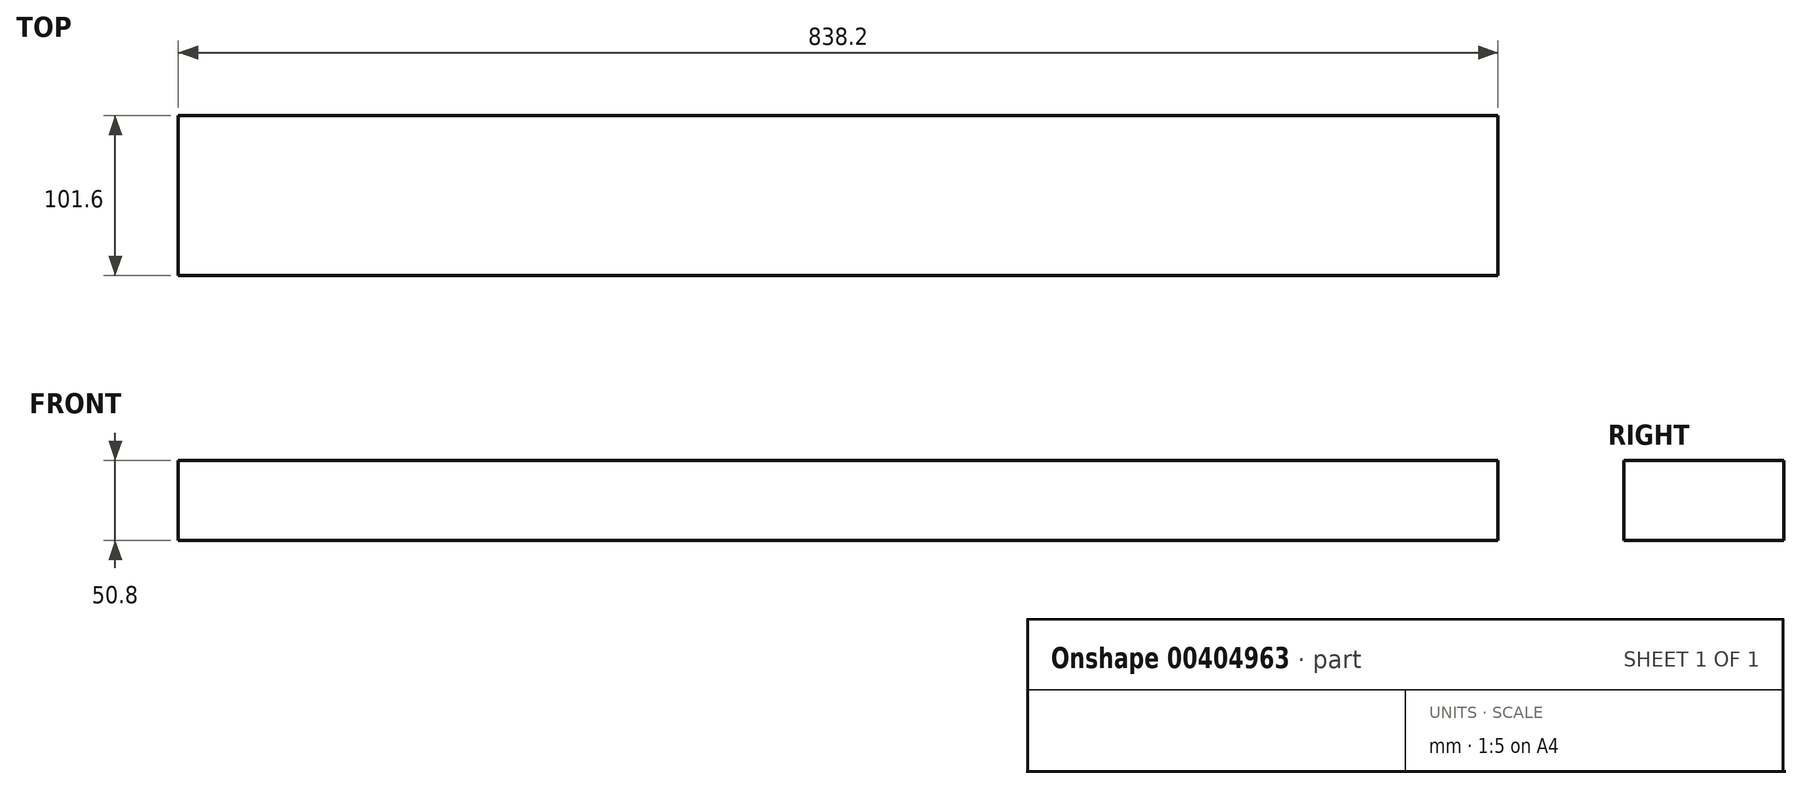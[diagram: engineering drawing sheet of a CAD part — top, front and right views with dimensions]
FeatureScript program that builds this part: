
annotation { "Feature Type Name" : "Feature", "Feature Type Description" : "" }
export const myFeature = defineFeature(function(context is Context, id is Id, definition is map)
    precondition{}
    {
        {
            var Q0;
            Q0=qCreatedBy(makeId("Right.planeOp"),FACE);
            var sketch = newSketch(context, id + "F0", { "sketchPlane" : qUnion([Q0])});
            skLineSegment(sketch, "E0.bottom", {"start": v(0, 0) * mm, "end": v(101.6, 0) * mm});
            skLineSegment(sketch, "E0.top", {"start": v(0, 50.8) * mm, "end": v(101.6, 50.8) * mm});
            skLineSegment(sketch, "E0.left", {"start": v(0, 0) * mm, "end": v(0, 50.8) * mm});
            skLineSegment(sketch, "E0.right", {"start": v(101.6, 0) * mm, "end": v(101.6, 50.8) * mm});
            skSolve(sketch);
        }
        {
            var Q0;
            Q0=qSketchRegion(id+"F0",true);
            extrude(context, id + "F1", {"entities" : qUnion([Q0]), "depth" : 838.2 * mm});
        }
    });
